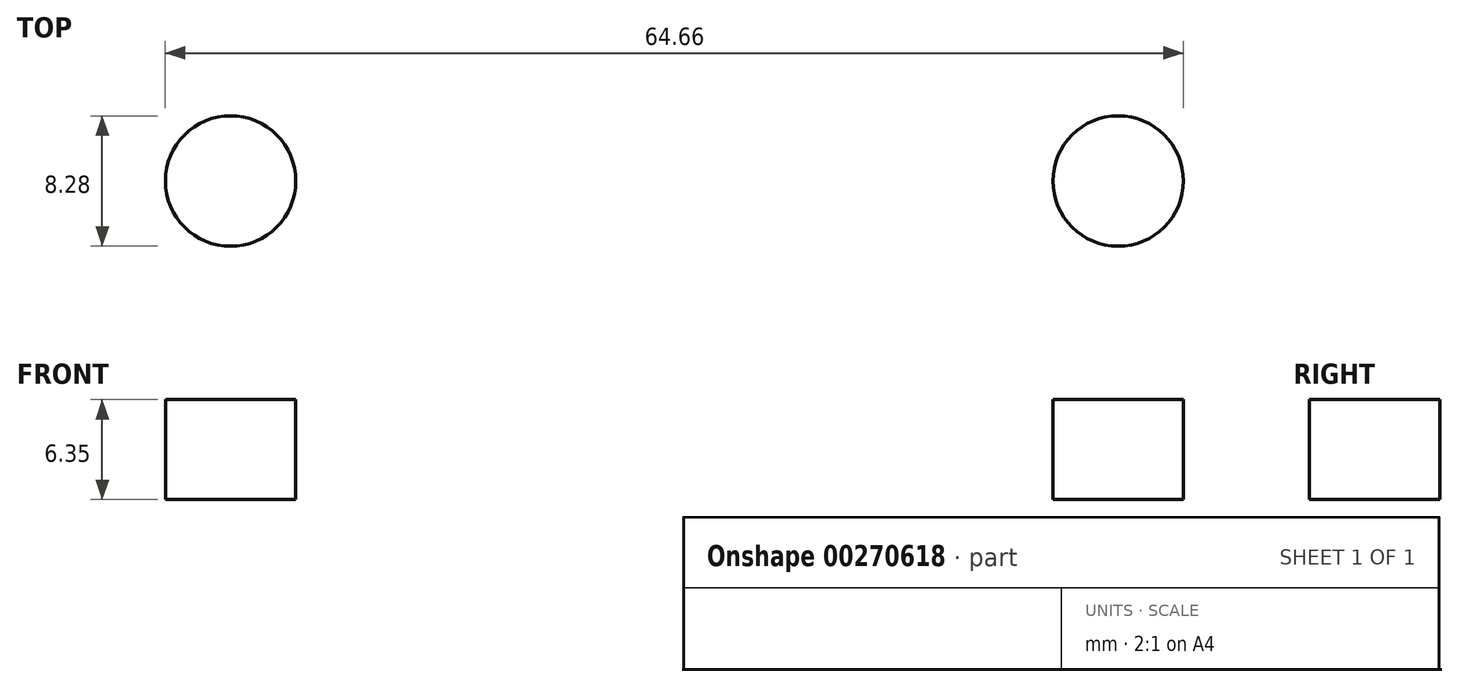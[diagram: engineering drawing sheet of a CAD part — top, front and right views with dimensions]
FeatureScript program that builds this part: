
annotation { "Feature Type Name" : "Feature", "Feature Type Description" : "" }
export const myFeature = defineFeature(function(context is Context, id is Id, definition is map)
    precondition{}
    {
        {
            var Q0;
            Q0=qCreatedBy(makeId("Top.planeOp"),FACE);
            var sketch = newSketch(context, id + "F0", { "sketchPlane" : qUnion([Q0])});
            skCircle(sketch, "E0", {"center": v(-33.75, 0) * mm, "radius": 4.14 * mm});
            skSolve(sketch);
        }
        {
            var Q0;
            Q0=qCreatedBy(makeId("Top.planeOp"),FACE);
            var sketch = newSketch(context, id + "F1", { "sketchPlane" : qUnion([Q0])});
            skCircle(sketch, "E1", {"center": v(22.62, 0) * mm, "radius": 4.14 * mm});
            skSolve(sketch);
        }
        {
            var Q0;
            Q0=makeQuery(id+"F0.imprint","IMPRINT",FACE,{"disambiguationData":[TD([[makeQuery(id+"F0.imprint","IMPRINT",EDGE,{"derivedFrom":sQuery(id+"F0.wireOp",EDGE,"E0")}),1.0]])]});
            var Q1;
            Q1=makeQuery(id+"F1.imprint","IMPRINT",FACE,{"disambiguationData":[TD([[makeQuery(id+"F1.imprint","IMPRINT",EDGE,{"derivedFrom":sQuery(id+"F1.wireOp",EDGE,"E1")}),1.0]])]});
            extrude(context, id + "F2", {"entities" : qUnion([Q0, Q1]), "depth" : 6.35 * mm});
        }
    });
